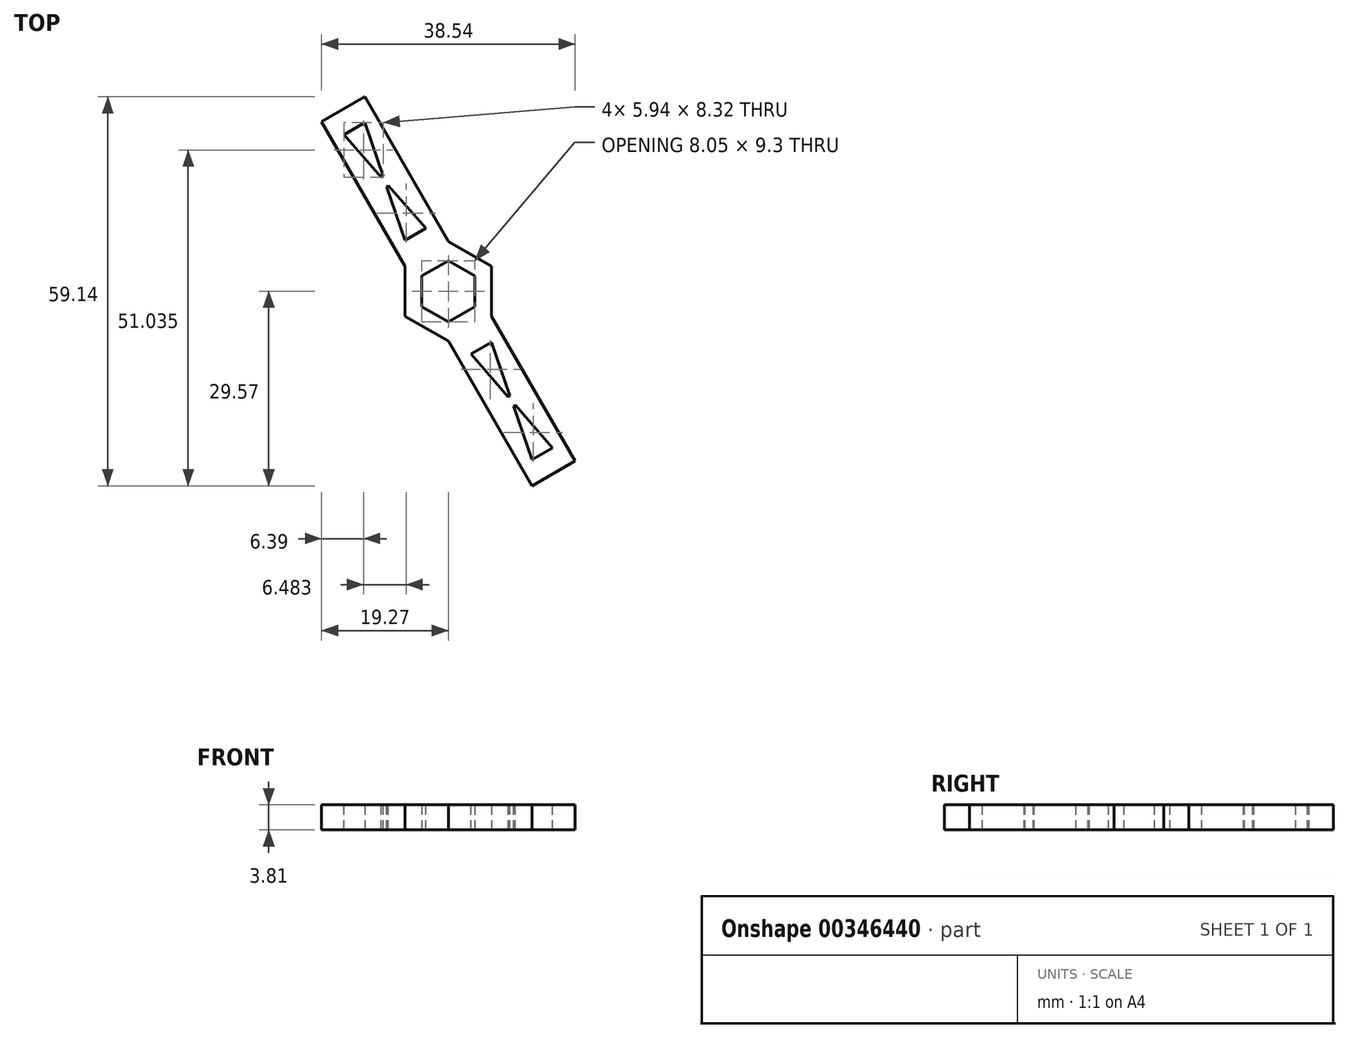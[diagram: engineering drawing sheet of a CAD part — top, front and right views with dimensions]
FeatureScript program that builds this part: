
annotation { "Feature Type Name" : "Feature", "Feature Type Description" : "" }
export const myFeature = defineFeature(function(context is Context, id is Id, definition is map)
    precondition{}
    {
        {
            var Q0;
            Q0=qCreatedBy(makeId("Top.planeOp"),FACE);
            var sketch = newSketch(context, id + "F0", { "sketchPlane" : qUnion([Q0])});
            skCircle(sketch, "E0.cCircle", {"center": v(0, 0) * mm, "radius": 4.03 * mm, "construction": true});
            skLineSegment(sketch, "E0.0", {"start": v(0, 4.65) * mm, "end": v(4.02, 2.33) * mm});
            skLineSegment(sketch, "E0.1", {"start": v(4.02, 2.33) * mm, "end": v(4.03, -2.32) * mm});
            skLineSegment(sketch, "E0.2", {"start": v(4.03, -2.32) * mm, "end": v(0, -4.65) * mm});
            skLineSegment(sketch, "E0.3", {"start": v(0, -4.65) * mm, "end": v(-4.02, -2.33) * mm});
            skLineSegment(sketch, "E0.4", {"start": v(-4.02, -2.33) * mm, "end": v(-4.03, 2.32) * mm});
            skLineSegment(sketch, "E0.5", {"start": v(-4.03, 2.32) * mm, "end": v(0, 4.65) * mm});
            skPoint(sketch, "E0.0.midPoint", {"position": v(2.01, 3.49) * mm});
            skCircle(sketch, "E1.cCircle", {"center": v(0, 0) * mm, "radius": 6.57 * mm, "construction": true});
            skLineSegment(sketch, "E1.0", {"start": v(0, 7.58) * mm, "end": v(6.56, 3.8) * mm});
            skLineSegment(sketch, "E1.1", {"start": v(6.56, 3.8) * mm, "end": v(6.57, -3.79) * mm});
            skLineSegment(sketch, "E1.2", {"start": v(6.57, -3.79) * mm, "end": v(0, -7.58) * mm});
            skLineSegment(sketch, "E1.3", {"start": v(0, -7.58) * mm, "end": v(-6.56, -3.8) * mm});
            skLineSegment(sketch, "E1.4", {"start": v(-6.56, -3.8) * mm, "end": v(-6.57, 3.79) * mm});
            skLineSegment(sketch, "E1.5", {"start": v(-6.57, 3.79) * mm, "end": v(0, 7.58) * mm});
            skPoint(sketch, "E1.0.midPoint", {"position": v(3.28, 5.69) * mm});
            skSolve(sketch);
        }
        {
            var Q0;
            Q0 = qSketchRegion(id + "F0", true);
            extrude(context, id + "F1", {"entities" : qUnion([Q0]), "depth" : 3.8 * mm});
        }
        {
            var Q0;
            Q0=makeQuery(id+"F1.opExtrude","SWEPT_FACE",FACE,{"disambiguationData":[OSD([sQuery(id+"F0.wireOp",EDGE,"E1.2")])]});
            extrude(context, id + "F2", {"entities" : qUnion([Q0]), "operationType" : NewBodyOperationType.ADD, "depth" : 25.4 * mm});
        }
        {
            var Q0;
            {var subQ0=sQuery(id+"F0.wireOp",EDGE,"E1.2");Q0=makeQuery(id+"F2.boolean.opBoolean","MERGE",FACE,{"derivedFrom":[makeQuery(id+"F1.opExtrude","CAP_FACE",FACE,{"disambiguationData":[OSD([sQuery(id+"F0.wireOp",EDGE,"E0.0"),sQuery(id+"F0.wireOp",EDGE,"E0.1"),sQuery(id+"F0.wireOp",EDGE,"E0.2"),sQuery(id+"F0.wireOp",EDGE,"E0.3"),sQuery(id+"F0.wireOp",EDGE,"E0.4"),sQuery(id+"F0.wireOp",EDGE,"E0.5"),sQuery(id+"F0.wireOp",EDGE,"E1.0"),sQuery(id+"F0.wireOp",EDGE,"E1.1"),subQ0,sQuery(id+"F0.wireOp",EDGE,"E1.3"),sQuery(id+"F0.wireOp",EDGE,"E1.4"),sQuery(id+"F0.wireOp",EDGE,"E1.5")])],"isStart":false}),makeQuery(id+"F2.opExtrude","SWEPT_FACE",FACE,{"disambiguationData":[OSD([subQ0]),TDD([makeQuery(id+"F1.opExtrude","CAP_EDGE",EDGE,{"disambiguationData":[OSD([subQ0])],"isStart":false})])]})]});}
            var sketch = newSketch(context, id + "F3", { "sketchPlane" : qUnion([Q0])});
            skLineSegment(sketch, "E2", {"start": v(6.36, -18.58) * mm, "end": v(12.92, -14.78) * mm});
            skLineSegment(sketch, "E3", {"start": v(9.64, -16.68) * mm, "end": v(14.28, -24.72) * mm});
            skLineSegment(sketch, "E4", {"start": v(14.28, -24.72) * mm, "end": v(12.7, -25.62) * mm});
            skLineSegment(sketch, "E5", {"start": v(12.7, -25.62) * mm, "end": v(8.07, -17.59) * mm});
            skPoint(sketch, "E6.endSnap0", {"position": v(16, -27.68) * mm});
            skLineSegment(sketch, "E7", {"start": v(14.28, -24.72) * mm, "end": v(15.85, -23.8) * mm});
            skLineSegment(sketch, "E8", {"start": v(15.85, -23.8) * mm, "end": v(9.64, -16.68) * mm});
            skLineSegment(sketch, "E9", {"start": v(12.7, -25.62) * mm, "end": v(9.64, -16.68) * mm});
            skLineSegment(sketch, "E10.MirrorCS", {"start": v(3.42, -9.55) * mm, "end": v(9.64, -16.68) * mm});
            skLineSegment(sketch, "E11.MirrorCS", {"start": v(6.57, -7.74) * mm, "end": v(9.64, -16.68) * mm});
            skLineSegment(sketch, "E12.MirrorCS", {"start": v(5, -8.65) * mm, "end": v(6.57, -7.74) * mm});
            skLineSegment(sketch, "E13.MirrorCS", {"start": v(5, -8.65) * mm, "end": v(3.42, -9.55) * mm});
            skLineSegment(sketch, "E14", {"start": v(9.9, -17.47) * mm, "end": v(9.1, -16.06) * mm});
            skLineSegment(sketch, "E15", {"start": v(9.1, -16.06) * mm, "end": v(9.37, -15.9) * mm});
            skLineSegment(sketch, "E16", {"start": v(9.37, -15.9) * mm, "end": v(10.18, -17.3) * mm});
            skLineSegment(sketch, "E17", {"start": v(9.9, -17.47) * mm, "end": v(10.18, -17.3) * mm});
            skSolve(sketch);
        }
        {
            var Q0;
            {var subQ0=sQuery(id+"F3.wireOp",EDGE,"E12.MirrorCS");Q0=makeQuery(id+"F3.imprint","IMPRINT",FACE,{"disambiguationData":[TD([[makeQuery(id+"F3.imprint","IMPRINT",EDGE,{"derivedFrom":subQ0}),-1.0]])]});}
            var Q1;
            {var subQ0=sQuery(id+"F3.wireOp",EDGE,"E4");Q1=makeQuery(id+"F3.imprint","IMPRINT",FACE,{"disambiguationData":[TD([[makeQuery(id+"F3.imprint","IMPRINT",EDGE,{"derivedFrom":subQ0}),-1.0]])]});}
            var Q2;
            {var subQ0=sQuery(id+"F3.wireOp",EDGE,"E7");Q2=makeQuery(id+"F3.imprint","IMPRINT",FACE,{"disambiguationData":[TD([[makeQuery(id+"F3.imprint","IMPRINT",EDGE,{"derivedFrom":subQ0}),1.0]])]});}
            extrude(context, id + "F4", {"entities" : qUnion([Q0, Q1, Q2]), "operationType" : NewBodyOperationType.REMOVE, "oppositeDirection" : true, "depth" : 25.4 * mm});
        }
        {
            var Q0;
            Q0=makeQuery(id+"F1.opExtrude","SWEPT_FACE",FACE,{"disambiguationData":[OSD([sQuery(id+"F0.wireOp",EDGE,"E1.5")])]});
            extrude(context, id + "F5", {"entities" : qUnion([Q0]), "operationType" : NewBodyOperationType.ADD, "depth" : 25.4 * mm});
        }
        {
            var Q0;
            {var subQ0=sQuery(id+"F0.wireOp",EDGE,"E1.5");var subQ1=sQuery(id+"F0.wireOp",EDGE,"E1.2");Q0=makeQuery(id+"F5.boolean.opBoolean","MERGE",FACE,{"derivedFrom":[makeQuery(id+"F2.boolean.opBoolean","MERGE",FACE,{"derivedFrom":[makeQuery(id+"F1.opExtrude","CAP_FACE",FACE,{"disambiguationData":[OSD([sQuery(id+"F0.wireOp",EDGE,"E0.0"),sQuery(id+"F0.wireOp",EDGE,"E0.1"),sQuery(id+"F0.wireOp",EDGE,"E0.2"),sQuery(id+"F0.wireOp",EDGE,"E0.3"),sQuery(id+"F0.wireOp",EDGE,"E0.4"),sQuery(id+"F0.wireOp",EDGE,"E0.5"),sQuery(id+"F0.wireOp",EDGE,"E1.0"),sQuery(id+"F0.wireOp",EDGE,"E1.1"),subQ1,sQuery(id+"F0.wireOp",EDGE,"E1.3"),sQuery(id+"F0.wireOp",EDGE,"E1.4"),subQ0])],"isStart":false}),makeQuery(id+"F2.opExtrude","SWEPT_FACE",FACE,{"disambiguationData":[OSD([subQ1]),TDD([makeQuery(id+"F1.opExtrude","CAP_EDGE",EDGE,{"disambiguationData":[OSD([subQ1])],"isStart":false})])]})]}),makeQuery(id+"F5.opExtrude","SWEPT_FACE",FACE,{"disambiguationData":[OSD([subQ0]),TDD([makeQuery(id+"F1.opExtrude","CAP_EDGE",EDGE,{"disambiguationData":[OSD([subQ0])],"isStart":false})])]})]});}
            var sketch = newSketch(context, id + "F6", { "sketchPlane" : qUnion([Q0])});
            skLineSegment(sketch, "E18", {"start": v(-4.02, -2.33) * mm, "end": v(4.02, 2.33) * mm});
            skLineSegment(sketch, "E19.0", {"start": v(3.42, -9.55) * mm, "end": v(9.1, -16.06) * mm});
            skLineSegment(sketch, "E19.1", {"start": v(3.42, -9.55) * mm, "end": v(6.57, -7.74) * mm});
            skLineSegment(sketch, "E19.2", {"start": v(6.57, -7.74) * mm, "end": v(9.37, -15.9) * mm});
            skLineSegment(sketch, "E19.3", {"start": v(15.85, -23.8) * mm, "end": v(10.18, -17.3) * mm});
            skLineSegment(sketch, "E19.4", {"start": v(12.7, -25.62) * mm, "end": v(9.9, -17.47) * mm});
            skLineSegment(sketch, "E19.5", {"start": v(15.85, -23.8) * mm, "end": v(12.7, -25.62) * mm});
            skLineSegment(sketch, "E19.6", {"start": v(9.9, -17.47) * mm, "end": v(10.18, -17.3) * mm});
            skLineSegment(sketch, "E19.7", {"start": v(9.1, -16.06) * mm, "end": v(9.37, -15.9) * mm});
            skLineSegment(sketch, "E20.MirrorCS", {"start": v(-6.57, 7.74) * mm, "end": v(-9.37, 15.9) * mm});
            skLineSegment(sketch, "E21.MirrorCS", {"start": v(-6.57, 7.74) * mm, "end": v(-3.42, 9.55) * mm});
            skLineSegment(sketch, "E22.MirrorCS", {"start": v(-3.42, 9.55) * mm, "end": v(-9.1, 16.06) * mm});
            skLineSegment(sketch, "E23.MirrorCS", {"start": v(-9.37, 15.9) * mm, "end": v(-9.1, 16.06) * mm});
            skLineSegment(sketch, "E24.MirrorCS", {"start": v(-12.7, 25.62) * mm, "end": v(-9.9, 17.47) * mm});
            skLineSegment(sketch, "E25.MirrorCS", {"start": v(-10.18, 17.3) * mm, "end": v(-9.9, 17.47) * mm});
            skLineSegment(sketch, "E26.MirrorCS", {"start": v(-15.85, 23.8) * mm, "end": v(-10.18, 17.3) * mm});
            skLineSegment(sketch, "E27.MirrorCS", {"start": v(-12.7, 25.62) * mm, "end": v(-15.85, 23.8) * mm});
            skSolve(sketch);
        }
        {
            var Q0;
            Q0 = qSketchRegion(id + "F6", true);
            extrude(context, id + "F7", {"entities" : qUnion([Q0]), "operationType" : NewBodyOperationType.REMOVE, "oppositeDirection" : true, "depth" : 25.4 * mm});
        }
    });
